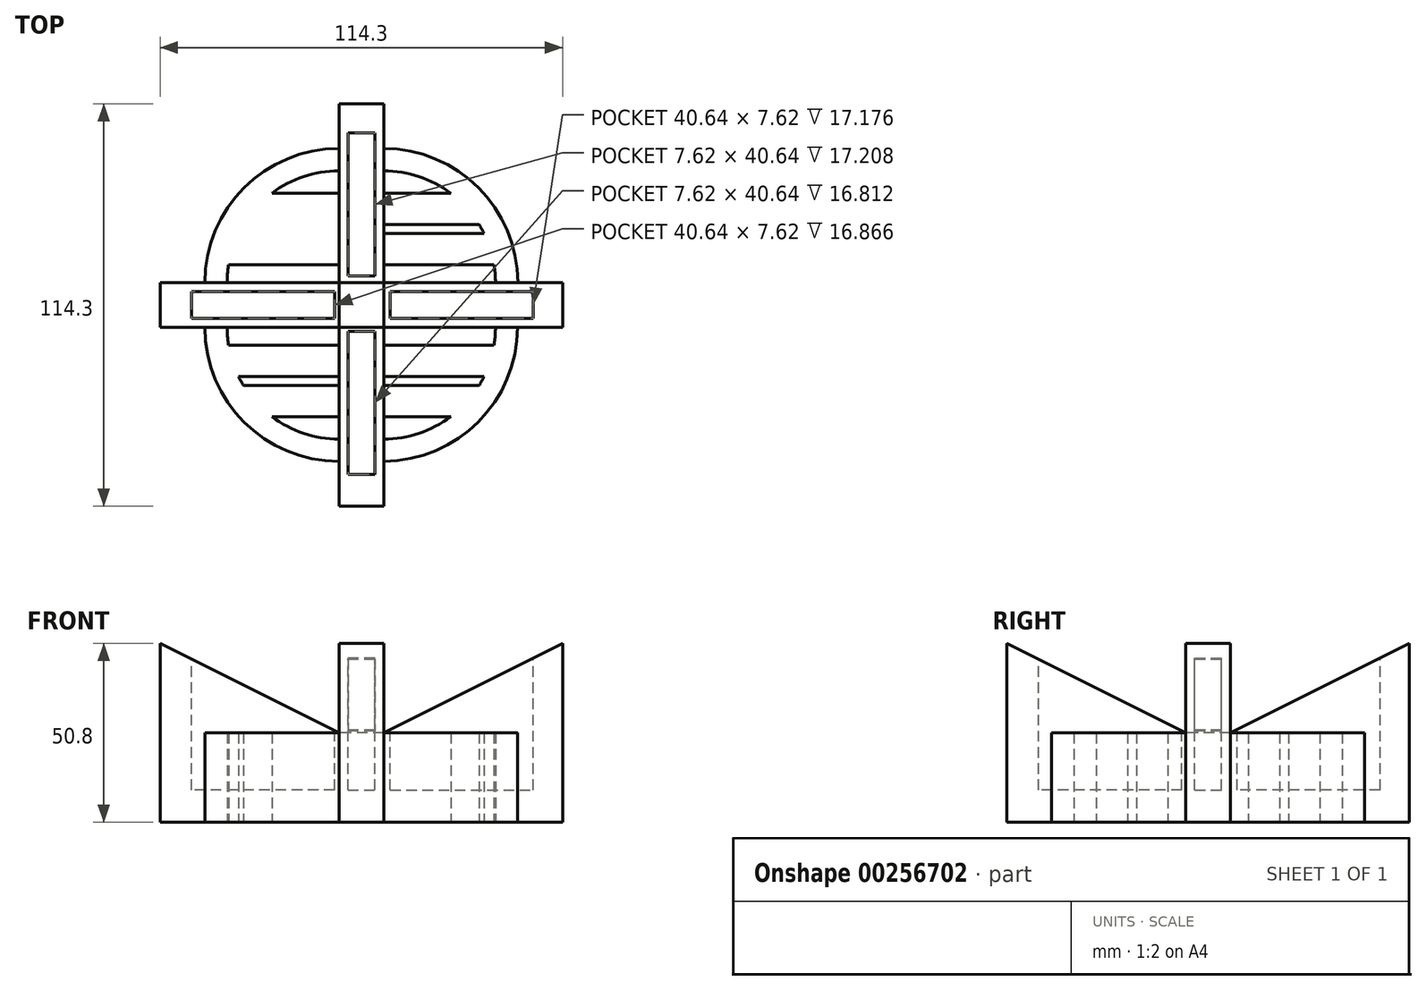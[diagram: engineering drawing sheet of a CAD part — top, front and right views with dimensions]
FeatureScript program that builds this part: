
annotation { "Feature Type Name" : "Feature", "Feature Type Description" : "" }
export const myFeature = defineFeature(function(context is Context, id is Id, definition is map)
    precondition{}
    {
        {
            var Q0;
            Q0=qCreatedBy(makeId("Top.planeOp"),FACE);
            var sketch = newSketch(context, id + "F0", { "sketchPlane" : qUnion([Q0])});
            skLineSegment(sketch, "E0.bottom", {"start": v(0, 0) * mm, "end": v(50.8, 0) * mm});
            skLineSegment(sketch, "E0.top", {"start": v(0, 12.7) * mm, "end": v(50.8, 12.7) * mm});
            skLineSegment(sketch, "E0.left", {"start": v(0, 0) * mm, "end": v(0, 12.7) * mm});
            skLineSegment(sketch, "E0.right", {"start": v(50.8, 0) * mm, "end": v(50.8, 12.7) * mm});
            skLineSegment(sketch, "E1.bottom", {"start": v(0, 12.7) * mm, "end": v(-12.7, 12.7) * mm});
            skLineSegment(sketch, "E1.top", {"start": v(0, 63.5) * mm, "end": v(-12.7, 63.5) * mm});
            skLineSegment(sketch, "E1.left", {"start": v(0, 12.7) * mm, "end": v(0, 63.5) * mm});
            skLineSegment(sketch, "E1.right", {"start": v(-12.7, 12.7) * mm, "end": v(-12.7, 63.5) * mm});
            skLineSegment(sketch, "E2.bottom", {"start": v(0, 0) * mm, "end": v(-12.7, 0) * mm});
            skLineSegment(sketch, "E2.top", {"start": v(0, -50.8) * mm, "end": v(-12.7, -50.8) * mm});
            skLineSegment(sketch, "E2.left", {"start": v(0, 0) * mm, "end": v(0, -50.8) * mm});
            skLineSegment(sketch, "E2.right", {"start": v(-12.7, 0) * mm, "end": v(-12.7, -50.8) * mm});
            skLineSegment(sketch, "E3.bottom", {"start": v(-12.7, 12.7) * mm, "end": v(-63.5, 12.7) * mm});
            skLineSegment(sketch, "E3.top", {"start": v(-12.7, 0) * mm, "end": v(-63.5, 0) * mm});
            skLineSegment(sketch, "E3.left", {"start": v(-12.7, 12.7) * mm, "end": v(-12.7, 0) * mm});
            skLineSegment(sketch, "E3.right", {"start": v(-63.5, 12.7) * mm, "end": v(-63.5, 0) * mm});
            skArc(sketch, "E4", {"start": v(-12.7, 50.8) * mm, "mid": v(-39.64, 39.64) * mm, "end": v(-50.8, 12.7) * mm});
            skArc(sketch, "E5", {"start": v(-12.7, 44.45) * mm, "mid": v(-35.15, 35.15) * mm, "end": v(-44.45, 12.7) * mm});
            skArc(sketch, "E6", {"start": v(-50.8, 0) * mm, "mid": v(-39.64, -26.94) * mm, "end": v(-12.7, -38.1) * mm});
            skArc(sketch, "E7", {"start": v(-44.45, 0) * mm, "mid": v(-44.35, -2.55) * mm, "end": v(-44.04, -5.08) * mm});
            skArc(sketch, "E8", {"start": v(0, -31.75) * mm, "mid": v(22.45, -22.45) * mm, "end": v(31.75, 0) * mm});
            skArc(sketch, "E9.trimOffspring", {"start": v(0, -38.05) * mm, "mid": v(26.88, -26.9) * mm, "end": v(38, 0) * mm});
            skArc(sketch, "E10", {"start": v(38.1, 12.7) * mm, "mid": v(26.94, 39.64) * mm, "end": v(0, 50.8) * mm});
            skArc(sketch, "E11", {"start": v(31.75, 12.7) * mm, "mid": v(22.45, 35.15) * mm, "end": v(0, 44.45) * mm});
            skLineSegment(sketch, "E12", {"start": v(-12.7, -5.08) * mm, "end": v(-44.04, -5.08) * mm});
            skLineSegment(sketch, "E13", {"start": v(-12.7, -13.97) * mm, "end": v(-41.21, -13.97) * mm});
            skArc(sketch, "E14.trimOffspring", {"start": v(-41.21, -13.97) * mm, "mid": v(-29.5, -26.94) * mm, "end": v(-12.7, -31.75) * mm});
            skLineSegment(sketch, "E15", {"start": v(-39.82, -16.51) * mm, "end": v(-12.7, -16.51) * mm});
            skLineSegment(sketch, "E16", {"start": v(-31.75, -25.4) * mm, "end": v(-12.7, -25.4) * mm});
            skLineSegment(sketch, "E17", {"start": v(0, 17.78) * mm, "end": v(31.34, 17.78) * mm});
            skLineSegment(sketch, "E18", {"start": v(0, 26.67) * mm, "end": v(28.51, 26.67) * mm});
            skLineSegment(sketch, "E19", {"start": v(0, 29.21) * mm, "end": v(27.12, 29.21) * mm});
            skLineSegment(sketch, "E20", {"start": v(0, 38.1) * mm, "end": v(19.05, 38.1) * mm});
            skLineSegment(sketch, "E21", {"start": v(-12.7, 17.78) * mm, "end": v(-44.04, 17.78) * mm});
            skLineSegment(sketch, "E22", {"start": v(-12.7, 26.67) * mm, "end": v(-41.21, 26.67) * mm});
            skLineSegment(sketch, "E23", {"start": v(-12.7, 38.1) * mm, "end": v(-31.75, 38.1) * mm});
            skLineSegment(sketch, "E24", {"start": v(0, -5.08) * mm, "end": v(31.34, -5.08) * mm});
            skLineSegment(sketch, "E25", {"start": v(0, -25.4) * mm, "end": v(19.05, -25.4) * mm});
            skLineSegment(sketch, "E26", {"start": v(0, -16.51) * mm, "end": v(27.12, -16.51) * mm});
            skLineSegment(sketch, "E27", {"start": v(0, -13.97) * mm, "end": v(28.51, -13.97) * mm});
            skSolve(sketch);
        }
        {
            var Q0;
            Q0=makeQuery(id+"F0.imprint","IMPRINT",FACE,{"disambiguationData":[TD([[makeQuery(id+"F0.imprint","IMPRINT",EDGE,{"derivedFrom":sQuery(id+"F0.wireOp",EDGE,"E0.bottom")}),1.0]])]});
            var Q1;
            Q1=makeQuery(id+"F0.imprint","IMPRINT",FACE,{"disambiguationData":[TD([[makeQuery(id+"F0.imprint","IMPRINT",EDGE,{"derivedFrom":sQuery(id+"F0.wireOp",EDGE,"E2.bottom")}),1.0]])]});
            var Q2;
            {var subQ1=sQuery(id+"F0.wireOp",EDGE,"E1.bottom");Q2=makeQuery(id+"F0.imprint","IMPRINT",FACE,{"disambiguationData":[TD([[makeQuery(id+"F0.imprint","IMPRINT",EDGE,{"derivedFrom":subQ1}),-1.0]])]});}
            var Q3;
            Q3=makeQuery(id+"F0.imprint","IMPRINT",FACE,{"disambiguationData":[TD([[makeQuery(id+"F0.imprint","IMPRINT",EDGE,{"derivedFrom":sQuery(id+"F0.wireOp",EDGE,"E3.top")}),-1.0]])]});
            var Q4;
            Q4=makeQuery(id+"F0.imprint","IMPRINT",FACE,{"disambiguationData":[TD([[makeQuery(id+"F0.imprint","IMPRINT",EDGE,{"derivedFrom":sQuery(id+"F0.wireOp",EDGE,"E0.left")}),1.0]])]});
            extrude(context, id + "F1", {"entities" : qUnion([Q0, Q1, Q2, Q3, Q4]), "depth" : 50.8 * mm});
        }
        {
            var Q0;
            Q0=makeQuery(id+"F1.opExtrude","SWEPT_FACE",FACE,{"disambiguationData":[OSD([sQuery(id+"F0.wireOp",EDGE,"E3.top")])]});
            var sketch = newSketch(context, id + "F2", { "sketchPlane" : qUnion([Q0])});
            skLineSegment(sketch, "E28", {"start": v(-12.7, 25.4) * mm, "end": v(-63.5, 50.8) * mm});
            skLineSegment(sketch, "E29", {"start": v(-63.5, 50.8) * mm, "end": v(-12.7, 50.8) * mm});
            skLineSegment(sketch, "E30", {"start": v(-12.7, 50.8) * mm, "end": v(-12.7, 25.4) * mm});
            skSolve(sketch);
        }
        {
            var Q0;
            Q0=makeQuery(id+"F2.imprint","IMPRINT",FACE,{"disambiguationData":[TD([[makeQuery(id+"F2.imprint","IMPRINT",EDGE,{"derivedFrom":sQuery(id+"F2.wireOp",EDGE,"E28")}),-1.0]])]});
            extrude(context, id + "F3", {"entities" : qUnion([Q0]), "operationType" : NewBodyOperationType.REMOVE, "oppositeDirection" : true, "depth" : 25.4 * mm});
        }
        {
            var Q0;
            Q0=makeQuery(id+"F3.boolean.opBoolean","MERGE",FACE,{"derivedFrom":[makeQuery(id+"F1.opExtrude","SWEPT_FACE",FACE,{"disambiguationData":[OSD([sQuery(id+"F0.wireOp",EDGE,"E1.right")])]}),makeQuery(id+"F1.opExtrude","SWEPT_FACE",FACE,{"disambiguationData":[OSD([sQuery(id+"F0.wireOp",EDGE,"E2.right")])]}),makeQuery(id+"F3.opExtrude","SWEPT_FACE",FACE,{"disambiguationData":[OSD([sQuery(id+"F2.wireOp",EDGE,"E30")])]})]});
            var sketch = newSketch(context, id + "F4", { "sketchPlane" : qUnion([Q0])});
            skLineSegment(sketch, "E31", {"start": v(0, 25.4) * mm, "end": v(50.8, 50.8) * mm});
            skLineSegment(sketch, "E32", {"start": v(50.8, 50.8) * mm, "end": v(0, 50.8) * mm});
            skLineSegment(sketch, "E33", {"start": v(0, 50.8) * mm, "end": v(0, 25.4) * mm});
            skSolve(sketch);
        }
        {
            var Q0;
            Q0 = qSketchRegion(id + "F4", true);
            extrude(context, id + "F5", {"entities" : qUnion([Q0]), "operationType" : NewBodyOperationType.REMOVE, "oppositeDirection" : true, "depth" : 25.4 * mm});
        }
        {
            var Q0;
            {var subQ3=sQuery(id+"F0.wireOp",EDGE,"E1.right");var subQ5=sQuery(id+"F0.wireOp",EDGE,"E2.right");var subQ6=makeQuery(id+"F1.opExtrude","SWEPT_FACE",FACE,{"disambiguationData":[OSD([subQ5])]});var subQ7=makeQuery(id+"F1.opExtrude","SWEPT_FACE",FACE,{"disambiguationData":[OSD([subQ3])]});var subQ13=sQuery(id+"F0.wireOp",EDGE,"E1.top");var subQ16=makeQuery(id+"F3.opExtrude","SWEPT_FACE",FACE,{"disambiguationData":[OSD([sQuery(id+"F2.wireOp",EDGE,"E30")])]});Q0=makeQuery(id+"F5.boolean.opBoolean","SPLIT",FACE,{"disambiguationData":[TD([makeQuery(id+"F1.opExtrude","SWEPT_FACE",FACE,{"disambiguationData":[OSD([subQ13])]})])],"derivedFrom":makeQuery(id+"F3.boolean.opBoolean","MERGE",FACE,{"derivedFrom":[subQ7,subQ6,subQ16]})});}
            var sketch = newSketch(context, id + "F6", { "sketchPlane" : qUnion([Q0])});
            skLineSegment(sketch, "E34", {"start": v(0, 25.4) * mm, "end": v(0, 50.8) * mm});
            skLineSegment(sketch, "E35", {"start": v(0, 50.8) * mm, "end": v(-63.5, 50.8) * mm});
            skLineSegment(sketch, "E36", {"start": v(-12.7, 25.4) * mm, "end": v(0, 25.4) * mm});
            skLineSegment(sketch, "E37", {"start": v(-12.7, 25.4) * mm, "end": v(-63.5, 50.8) * mm});
            skSolve(sketch);
        }
        {
            var Q0;
            Q0 = qSketchRegion(id + "F6", true);
            extrude(context, id + "F7", {"entities" : qUnion([Q0]), "operationType" : NewBodyOperationType.REMOVE, "oppositeDirection" : true, "depth" : 12.7 * mm});
        }
        {
            var Q0;
            Q0=makeQuery(id+"F1.opExtrude","SWEPT_FACE",FACE,{"disambiguationData":[OSD([sQuery(id+"F0.wireOp",EDGE,"E0.top")])]});
            var sketch = newSketch(context, id + "F8", { "sketchPlane" : qUnion([Q0])});
            skLineSegment(sketch, "E38", {"start": v(0, 25.4) * mm, "end": v(-50.8, 50.8) * mm});
            skLineSegment(sketch, "E39", {"start": v(-50.8, 50.8) * mm, "end": v(0, 50.8) * mm});
            skLineSegment(sketch, "E40", {"start": v(0, 50.8) * mm, "end": v(0, 25.4) * mm});
            skSolve(sketch);
        }
        {
            var Q0;
            Q0 = qSketchRegion(id + "F8", true);
            extrude(context, id + "F9", {"entities" : qUnion([Q0]), "operationType" : NewBodyOperationType.REMOVE, "oppositeDirection" : true, "depth" : 25.4 * mm});
        }
        {
            var Q0;
            {var subQ3=sQuery(id+"F0.wireOp",EDGE,"E1.bottom");Q0=makeQuery(id+"F0.imprint","IMPRINT",FACE,{"disambiguationData":[TD([[makeQuery(id+"F0.imprint","IMPRINT",EDGE,{"derivedFrom":subQ3}),-1.0]])]});}
            cPlane(context, id + "F10", {"entities" : qUnion([Q0]), "cplaneType" : CPlaneType.OFFSET, "offset" : 52.32 * mm, "width" : 152.4 * mm, "height" : 152.4 * mm});
        }
        {
            var Q0;
            Q0=qCreatedBy(id+"F10.planeOp",FACE);
            var sketch = newSketch(context, id + "F11", { "sketchPlane" : qUnion([Q0])});
            skLineSegment(sketch, "E41", {"start": v(-10.16, 14.6) * mm, "end": v(-2.54, 14.6) * mm});
            skLineSegment(sketch, "E42", {"start": v(-2.54, 14.6) * mm, "end": v(-2.54, 55.24) * mm});
            skLineSegment(sketch, "E43", {"start": v(-2.54, 55.24) * mm, "end": v(-10.16, 55.24) * mm});
            skLineSegment(sketch, "E44", {"start": v(-10.16, 55.24) * mm, "end": v(-10.16, 14.6) * mm});
            skSolve(sketch);
        }
        {
            var Q0;
            {var subQ0=sQuery(id+"F0.wireOp",EDGE,"E8");Q0=makeQuery(id+"F0.imprint","IMPRINT",FACE,{"disambiguationData":[TD([[makeQuery(id+"F0.imprint","IMPRINT",EDGE,{"derivedFrom":subQ0}),-1.0]])]});}
            var Q1;
            {var subQ0=sQuery(id+"F0.wireOp",EDGE,"E10");Q1=makeQuery(id+"F0.imprint","IMPRINT",FACE,{"disambiguationData":[TD([[makeQuery(id+"F0.imprint","IMPRINT",EDGE,{"derivedFrom":subQ0}),1.0]])]});}
            var Q2;
            {var subQ0=sQuery(id+"F0.wireOp",EDGE,"E6");Q2=makeQuery(id+"F0.imprint","IMPRINT",FACE,{"disambiguationData":[TD([[makeQuery(id+"F0.imprint","IMPRINT",EDGE,{"derivedFrom":subQ0}),1.0]])]});}
            var Q3;
            {var subQ0=sQuery(id+"F0.wireOp",EDGE,"E4");Q3=makeQuery(id+"F0.imprint","IMPRINT",FACE,{"disambiguationData":[TD([[makeQuery(id+"F0.imprint","IMPRINT",EDGE,{"derivedFrom":subQ0}),1.0]])]});}
            var Q4;
            {var subQ0=sQuery(id+"F0.wireOp",EDGE,"1GBCUqj0-Gwa4-Qe7o-IT9H-josLuibStq1u");Q4=makeQuery(id+"F0.imprint","IMPRINT",FACE,{"disambiguationData":[TD([[makeQuery(id+"F0.imprint","IMPRINT",EDGE,{"derivedFrom":subQ0}),1.0]])]});}
            var Q5;
            {var subQ0=sQuery(id+"F0.wireOp",EDGE,"oSknAzFa-AiGw-QtbJ-bBPK-adncSnHilFg1");Q5=makeQuery(id+"F0.imprint","IMPRINT",FACE,{"disambiguationData":[TD([[makeQuery(id+"F0.imprint","IMPRINT",EDGE,{"derivedFrom":subQ0}),-1.0]])]});}
            var Q6;
            {var subQ0=sQuery(id+"F0.wireOp",EDGE,"E15");Q6=makeQuery(id+"F0.imprint","IMPRINT",FACE,{"disambiguationData":[TD([[makeQuery(id+"F0.imprint","IMPRINT",EDGE,{"derivedFrom":subQ0}),-1.0]])]});}
            var Q7;
            {var subQ0=sQuery(id+"F0.wireOp",EDGE,"E19");Q7=makeQuery(id+"F0.imprint","IMPRINT",FACE,{"disambiguationData":[TD([[makeQuery(id+"F0.imprint","IMPRINT",EDGE,{"derivedFrom":subQ0}),1.0]])]});}
            var Q8;
            {var subQ0=sQuery(id+"F0.wireOp",EDGE,"E17");Q8=makeQuery(id+"F0.imprint","IMPRINT",FACE,{"disambiguationData":[TD([[makeQuery(id+"F0.imprint","IMPRINT",EDGE,{"derivedFrom":subQ0}),1.0]])]});}
            var Q9;
            {var subQ0=sQuery(id+"F0.wireOp",EDGE,"LgsJRNul-5dfk-TY1h-Da5b-ulKWO6Mn2mF3");Q9=makeQuery(id+"F0.imprint","IMPRINT",FACE,{"disambiguationData":[TD([[makeQuery(id+"F0.imprint","IMPRINT",EDGE,{"derivedFrom":subQ0}),1.0]])]});}
            var Q10;
            {var subQ0=sQuery(id+"F0.wireOp",EDGE,"V7UPe2Lr-m44r-uz1S-9QeL-VjLSorqZxGK8");Q10=makeQuery(id+"F0.imprint","IMPRINT",FACE,{"disambiguationData":[TD([[makeQuery(id+"F0.imprint","IMPRINT",EDGE,{"derivedFrom":subQ0}),-1.0]])]});}
            var Q11;
            {var subQ0=sQuery(id+"F0.wireOp",EDGE,"E22");Q11=makeQuery(id+"F0.imprint","IMPRINT",FACE,{"disambiguationData":[TD([[makeQuery(id+"F0.imprint","IMPRINT",EDGE,{"derivedFrom":subQ0}),-1.0]])]});}
            var Q12;
            {var subQ0=sQuery(id+"F0.wireOp",EDGE,"E21");Q12=makeQuery(id+"F0.imprint","IMPRINT",FACE,{"disambiguationData":[TD([[makeQuery(id+"F0.imprint","IMPRINT",EDGE,{"derivedFrom":subQ0}),-1.0]])]});}
            var Q13;
            {var subQ0=sQuery(id+"F0.wireOp",EDGE,"E24");Q13=makeQuery(id+"F0.imprint","IMPRINT",FACE,{"disambiguationData":[TD([[makeQuery(id+"F0.imprint","IMPRINT",EDGE,{"derivedFrom":subQ0}),-1.0]])]});}
            var Q14;
            {var subQ0=sQuery(id+"F0.wireOp",EDGE,"E25");Q14=makeQuery(id+"F0.imprint","IMPRINT",FACE,{"disambiguationData":[TD([[makeQuery(id+"F0.imprint","IMPRINT",EDGE,{"derivedFrom":subQ0}),1.0]])]});}
            extrude(context, id + "F12", {"entities" : qUnion([Q0, Q1, Q2, Q3, Q4, Q5, Q6, Q7, Q8, Q9, Q10, Q11, Q12, Q13, Q14]), "operationType" : NewBodyOperationType.ADD, "depth" : 25.4 * mm});
        }
        {
            var Q0;
            Q0=qCreatedBy(id+"F10.planeOp",FACE);
            var sketch = newSketch(context, id + "F13", { "sketchPlane" : qUnion([Q0])});
            skLineSegment(sketch, "E45.bottom", {"start": v(1.84, 2.54) * mm, "end": v(42.48, 2.54) * mm});
            skLineSegment(sketch, "E45.top", {"start": v(1.84, 10.16) * mm, "end": v(42.48, 10.16) * mm});
            skLineSegment(sketch, "E45.left", {"start": v(1.84, 2.54) * mm, "end": v(1.84, 10.16) * mm});
            skLineSegment(sketch, "E45.right", {"start": v(42.48, 2.54) * mm, "end": v(42.48, 10.16) * mm});
            skSolve(sketch);
        }
        {
            var Q0;
            Q0=qCreatedBy(id+"F10.planeOp",FACE);
            var sketch = newSketch(context, id + "F14", { "sketchPlane" : qUnion([Q0])});
            skLineSegment(sketch, "E46.bottom", {"start": v(-13.92, 2.54) * mm, "end": v(-54.56, 2.54) * mm});
            skLineSegment(sketch, "E46.top", {"start": v(-13.92, 10.16) * mm, "end": v(-54.56, 10.16) * mm});
            skLineSegment(sketch, "E46.left", {"start": v(-13.92, 2.54) * mm, "end": v(-13.92, 10.16) * mm});
            skLineSegment(sketch, "E46.right", {"start": v(-54.56, 2.54) * mm, "end": v(-54.56, 10.16) * mm});
            skSolve(sketch);
        }
        {
            var Q0;
            Q0=qCreatedBy(id+"F10.planeOp",FACE);
            var sketch = newSketch(context, id + "F15", { "sketchPlane" : qUnion([Q0])});
            skLineSegment(sketch, "E47.bottom", {"start": v(-10.16, -1.11) * mm, "end": v(-2.54, -1.11) * mm});
            skLineSegment(sketch, "E47.top", {"start": v(-10.16, -41.75) * mm, "end": v(-2.54, -41.75) * mm});
            skLineSegment(sketch, "E47.left", {"start": v(-10.16, -1.11) * mm, "end": v(-10.16, -41.75) * mm});
            skLineSegment(sketch, "E47.right", {"start": v(-2.54, -1.11) * mm, "end": v(-2.54, -41.75) * mm});
            skSolve(sketch);
        }
        {
            var Q0;
            Q0=makeQuery(id+"F13.imprint","IMPRINT",FACE,{"disambiguationData":[TD([[makeQuery(id+"F13.imprint","IMPRINT",EDGE,{"derivedFrom":sQuery(id+"F13.wireOp",EDGE,"E45.bottom")}),1.0]])]});
            var Q1;
            Q1=makeQuery(id+"F15.imprint","IMPRINT",FACE,{"disambiguationData":[TD([[makeQuery(id+"F15.imprint","IMPRINT",EDGE,{"derivedFrom":sQuery(id+"F15.wireOp",EDGE,"E47.bottom")}),-1.0]])]});
            var Q2;
            Q2=makeQuery(id+"F11.imprint","IMPRINT",FACE,{"disambiguationData":[TD([[makeQuery(id+"F11.imprint","IMPRINT",EDGE,{"derivedFrom":sQuery(id+"F11.wireOp",EDGE,"E41")}),1.0]])]});
            var Q3;
            Q3=makeQuery(id+"F14.imprint","IMPRINT",FACE,{"disambiguationData":[TD([[makeQuery(id+"F14.imprint","IMPRINT",EDGE,{"derivedFrom":sQuery(id+"F14.wireOp",EDGE,"E46.bottom")}),-1.0]])]});
            extrude(context, id + "F16", {"entities" : qUnion([Q0, Q1, Q2, Q3]), "operationType" : NewBodyOperationType.REMOVE, "oppositeDirection" : true, "depth" : 43.18 * mm});
        }
    });
